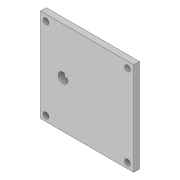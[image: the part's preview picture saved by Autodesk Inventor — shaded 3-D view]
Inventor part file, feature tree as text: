
AUTODESK INVENTOR PART (.ipt)
format: ipt  version: 2019 (Build 230136000, 136)  size: 126,976 bytes
history: native  units: in
note: dims shown in document units (in); Inventor stores cm internally (conversion verified against a paired STEP export)
features: sketch x7, extrude x4
ambient origin geometry x8: Origin, YZ Plane, XZ Plane, XY Plane, X Axis, Y Axis, Z Axis, Center Point
bodies: Solid1 (feature_tree)
feature tree (11):
  extrude  "Extrusion1"  Depth=6.2992in
  sketch  "Sketch2"  dims[d2=0.3937in d3=0.0in d4=0.3937in]
  extrude  "Extrusion2"  Depth=0.3937in
  extrude  "Extrusion3"  Depth=5.5118in
  sketch  "Sketch5"  dims[d9=2.7559in]
  sketch  "Sketch6"  dims[d10=5.5118in]
  extrude  "Extrusion4"  Depth=5.5118in
  sketch  "Sketch1"  dims[d0=6.2992in d1=6.2992in]
  sketch  "Sketch3"  dims[d5=5.9055in d6=5.5118in]
  sketch  "Sketch4"  dims[d7=5.5118in d8=5.5118in]
  sketch  "Sketch7"  dims[d11=0.3937in d12=0.3937in d14=0.3937in d15=0.3937in d17=0.3937in d18=0.0in d19=1.1811in d21=0.0in d22=0.0in d23=0.3937in d24=5.9055in d25=0.3937in d26=5.9055in d27=5.5118in d28=5.5118in d29=5.5118in d30=0.3937in d31=0.3937in d32=0.3937in d33=0.3937in d34=0.0in d35=0.0in d36=0.1181in d40=0.6693in]
